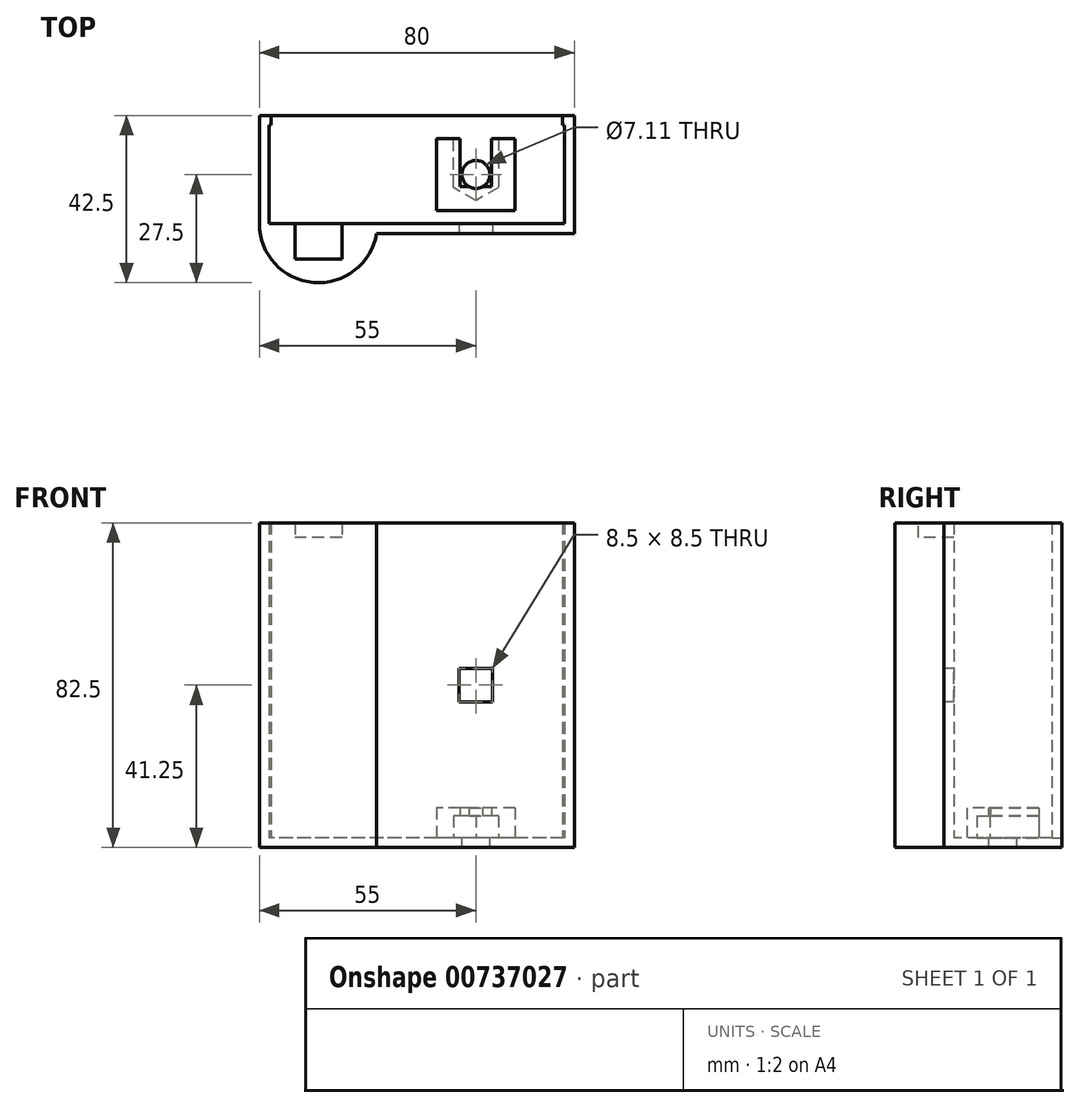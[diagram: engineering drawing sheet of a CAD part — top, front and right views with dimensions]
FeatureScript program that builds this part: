
annotation { "Feature Type Name" : "Feature", "Feature Type Description" : "" }
export const myFeature = defineFeature(function(context is Context, id is Id, definition is map)
    precondition{}
    {
        {
            assignVariable(context, id + "F0", {"name" : "shell_thickness", "anyValue" : 2.5 * mm});
        }
        {
            var Q0;
            Q0=qCreatedBy(makeId("Top.planeOp"),FACE);
            var sketch = newSketch(context, id + "F1", { "sketchPlane" : qUnion([Q0])});
            skLineSegment(sketch, "E0.bottom", {"start": v(37.5, 12.5) * mm, "end": v(-37.5, 12.5) * mm});
            skLineSegment(sketch, "E0.top", {"start": v(37.5, -12.5) * mm, "end": v(-37.5, -12.5) * mm});
            skLineSegment(sketch, "E0.left", {"start": v(37.5, 12.5) * mm, "end": v(37.5, -12.5) * mm});
            skLineSegment(sketch, "E0.right", {"start": v(-37.5, 12.5) * mm, "end": v(-37.5, -12.5) * mm});
            skPoint(sketch, "E0.middle", {"position": v(0, 0) * mm});
            skArc(sketch, "E1", {"start": v(-37.5, -12.5) * mm, "mid": v(-25, -25) * mm, "end": v(-12.5, -12.5) * mm});
            skLineSegment(sketch, "E2.0", {"start": v(-40, 15) * mm, "end": v(-40, -12.5) * mm});
            skLineSegment(sketch, "E2.1", {"start": v(40, 15) * mm, "end": v(-40, 15) * mm});
            skArc(sketch, "E2.2", {"start": v(-40, -12.5) * mm, "mid": v(-26.25, -27.45) * mm, "end": v(-10.2, -15) * mm});
            skLineSegment(sketch, "E2.3", {"start": v(40, -15) * mm, "end": v(-10.2, -15) * mm});
            skLineSegment(sketch, "E2.4", {"start": v(40, 15) * mm, "end": v(40, -15) * mm});
            skLineSegment(sketch, "E3", {"start": v(-37, 12.5) * mm, "end": v(-37, 15) * mm});
            skLineSegment(sketch, "E4", {"start": v(37, 12.5) * mm, "end": v(37, 15) * mm});
            skSolve(sketch);
        }
        {
            var Q0;
            Q0=makeQuery(id+"F1.imprint","IMPRINT",FACE,{"disambiguationData":[TD([[makeQuery(id+"F1.imprint","IMPRINT",EDGE,{"derivedFrom":sQuery(id+"F1.wireOp",EDGE,"E0.bottom")}),1.0]])]});
            var Q1;
            Q1=makeQuery(id+"F1.imprint","IMPRINT",FACE,{"disambiguationData":[TD([[makeQuery(id+"F1.imprint","IMPRINT",EDGE,{"derivedFrom":sQuery(id+"F1.wireOp",EDGE,"E0.bottom")}),-1.0]])]});
            var Q2;
            {var subQ0=sQuery(id+"F1.wireOp",EDGE,"E3");Q2=makeQuery(id+"F1.imprint","IMPRINT",FACE,{"disambiguationData":[TD([[makeQuery(id+"F1.imprint","IMPRINT",EDGE,{"derivedFrom":subQ0}),-1.0]])]});}
            var Q3;
            {var subQ0=sQuery(id+"F1.wireOp",EDGE,"E1");Q3=makeQuery(id+"F1.imprint","IMPRINT",FACE,{"disambiguationData":[TD([[makeQuery(id+"F1.imprint","IMPRINT",EDGE,{"derivedFrom":subQ0}),1.0]])]});}
            extrude(context, id + "F2", {"entities" : qUnion([Q0, Q1, Q2, Q3]), "oppositeDirection" : true, "depth" : getVariable(context, 'shell_thickness'), "offsetDistance" : 25 * mm});
        }
        {
            var Q0;
            {var subQ7=sQuery(id+"F1.wireOp",EDGE,"E0.left");Q0=makeQuery(id+"F1.imprint","IMPRINT",FACE,{"disambiguationData":[TD([[makeQuery(id+"F1.imprint","IMPRINT",EDGE,{"derivedFrom":subQ7}),1.0]])]});}
            var Q1;
            {var subQ0=sQuery(id+"F1.wireOp",EDGE,"E1");Q1=makeQuery(id+"F1.imprint","IMPRINT",FACE,{"disambiguationData":[TD([[makeQuery(id+"F1.imprint","IMPRINT",EDGE,{"derivedFrom":subQ0}),1.0]])]});}
            extrude(context, id + "F3", {"entities" : qUnion([Q0, Q1]), "operationType" : NewBodyOperationType.ADD, "depth" : 80 * mm, "offsetDistance" : 25 * mm});
        }
        {
            var Q0;
            Q0=makeQuery(id+"F3.opExtrude","CAP_FACE",FACE,{"disambiguationData":[OSD([sQuery(id+"F1.wireOp",EDGE,"E0.bottom"),sQuery(id+"F1.wireOp",EDGE,"E0.top"),sQuery(id+"F1.wireOp",EDGE,"E0.left"),sQuery(id+"F1.wireOp",EDGE,"E0.right"),sQuery(id+"F1.wireOp",EDGE,"E2.0"),sQuery(id+"F1.wireOp",EDGE,"E2.1"),sQuery(id+"F1.wireOp",EDGE,"E2.2"),sQuery(id+"F1.wireOp",EDGE,"E2.3"),sQuery(id+"F1.wireOp",EDGE,"E2.4"),sQuery(id+"F1.wireOp",EDGE,"E3"),sQuery(id+"F1.wireOp",EDGE,"E4")])],"isStart":false});
            var sketch = newSketch(context, id + "F4", { "sketchPlane" : qUnion([Q0])});
            skCircle(sketch, "E5", {"center": v(-25, -12.5) * mm, "radius": 12.5 * mm, "construction": true});
            skLineSegment(sketch, "E6.bottom", {"start": v(-19, -9.5) * mm, "end": v(-31, -9.5) * mm});
            skLineSegment(sketch, "E6.top", {"start": v(-19, -21.5) * mm, "end": v(-31, -21.5) * mm});
            skLineSegment(sketch, "E6.left", {"start": v(-19, -9.5) * mm, "end": v(-19, -21.5) * mm});
            skLineSegment(sketch, "E6.right", {"start": v(-31, -9.5) * mm, "end": v(-31, -21.5) * mm});
            skPoint(sketch, "E6.middle", {"position": v(-25, -15.5) * mm});
            skSolve(sketch);
        }
        {
            var Q0;
            Q0 = qSketchRegion(id + "F4", true);
            extrude(context, id + "F5", {"entities" : qUnion([Q0]), "operationType" : NewBodyOperationType.REMOVE, "oppositeDirection" : true, "depth" : 3.75 * mm, "offsetDistance" : 25 * mm});
        }
        {
            var Q0;
            {var subQ0=sQuery(id+"F1.wireOp",EDGE,"E2.3");Q0=makeQuery(id+"F3.boolean.opBoolean","MERGE",FACE,{"derivedFrom":[makeQuery(id+"F2.opExtrude","SWEPT_FACE",FACE,{"disambiguationData":[OSD([subQ0])]}),makeQuery(id+"F3.opExtrude","SWEPT_FACE",FACE,{"disambiguationData":[OSD([subQ0])]})]});}
            var sketch = newSketch(context, id + "F6", { "sketchPlane" : qUnion([Q0])});
            skPoint(sketch, "E7.middle.positionSnap0", {"position": v(40, 38.75) * mm});
            skPoint(sketch, "E7.middle.positionSnap1", {"position": v(14.9, -2.5) * mm});
            skPoint(sketch, "E7.centerSnap0", {"position": v(40, 38.75) * mm});
            skPoint(sketch, "E7.centerSnap1", {"position": v(14.9, -2.5) * mm});
            skLineSegment(sketch, "E8.bottom", {"start": v(19.25, 43) * mm, "end": v(10.75, 43) * mm});
            skLineSegment(sketch, "E8.top", {"start": v(19.25, 34.5) * mm, "end": v(10.75, 34.5) * mm});
            skLineSegment(sketch, "E8.left", {"start": v(19.25, 43) * mm, "end": v(19.25, 34.5) * mm});
            skLineSegment(sketch, "E8.right", {"start": v(10.75, 43) * mm, "end": v(10.75, 34.5) * mm});
            skPoint(sketch, "E8.middle", {"position": v(15, 38.75) * mm});
            skSolve(sketch);
        }
        {
            var Q0;
            Q0=makeQuery(id+"F6.imprint","IMPRINT",FACE,{"disambiguationData":[TD([[makeQuery(id+"F6.imprint","IMPRINT",EDGE,{"derivedFrom":sQuery(id+"F6.wireOp",EDGE,"E8.bottom")}),1.0]])]});
            extrude(context, id + "F7", {"entities" : qUnion([Q0]), "operationType" : NewBodyOperationType.REMOVE, "endBound" : BoundingType.UP_TO_NEXT, "oppositeDirection" : true, "depth" : 25 * mm, "offsetDistance" : 25 * mm});
        }
        {
            var Q0;
            {var subQ0=sQuery(id+"F1.wireOp",EDGE,"E0.left");Q0=makeQuery(id+"F1.imprint","IMPRINT",FACE,{"disambiguationData":[TD([[makeQuery(id+"F1.imprint","IMPRINT",EDGE,{"derivedFrom":subQ0}),-1.0]])]});}
            var sketch = newSketch(context, id + "F8", { "sketchPlane" : qUnion([Q0])});
            skCircle(sketch, "E9.cCircle", {"center": v(15, 0) * mm, "radius": 5.72 * mm, "construction": true});
            skLineSegment(sketch, "E9.0", {"start": v(9.29, -3.3) * mm, "end": v(9.29, 3.3) * mm});
            skLineSegment(sketch, "E9.1", {"start": v(9.29, 3.3) * mm, "end": v(15, 6.6) * mm});
            skLineSegment(sketch, "E9.2", {"start": v(15, 6.6) * mm, "end": v(20.71, 3.3) * mm});
            skLineSegment(sketch, "E9.3", {"start": v(20.71, 3.3) * mm, "end": v(20.71, -3.3) * mm});
            skLineSegment(sketch, "E9.4", {"start": v(20.71, -3.3) * mm, "end": v(15, -6.6) * mm});
            skLineSegment(sketch, "E9.5", {"start": v(15, -6.6) * mm, "end": v(9.29, -3.3) * mm});
            skPoint(sketch, "E9.0.midPoint", {"position": v(9.29, 0) * mm});
            skCircle(sketch, "E10", {"center": v(15, 0) * mm, "radius": 3.56 * mm});
            skLineSegment(sketch, "E11.bottom", {"start": v(25, 9.11) * mm, "end": v(19, 9.11) * mm});
            skLineSegment(sketch, "E11.top", {"start": v(25, -9.11) * mm, "end": v(5, -9.11) * mm});
            skLineSegment(sketch, "E11.left", {"start": v(25, 9.11) * mm, "end": v(25, -9.11) * mm});
            skLineSegment(sketch, "E11.right", {"start": v(5, 9.11) * mm, "end": v(5, -9.11) * mm});
            skLineSegment(sketch, "E12.top", {"start": v(19, -3.11) * mm, "end": v(11, -3.11) * mm});
            skLineSegment(sketch, "E12.left", {"start": v(19, 3.11) * mm, "end": v(19, -3.11) * mm});
            skLineSegment(sketch, "E12.right", {"start": v(11, 3.11) * mm, "end": v(11, -3.11) * mm});
            skLineSegment(sketch, "E13", {"start": v(11, 3.11) * mm, "end": v(11, 9.11) * mm});
            skLineSegment(sketch, "E14", {"start": v(19, 3.11) * mm, "end": v(19, 9.11) * mm});
            skLineSegment(sketch, "E15.trimOffspring", {"start": v(11, 9.11) * mm, "end": v(5, 9.11) * mm});
            skLineSegment(sketch, "E16", {"start": v(9.29, 3.3) * mm, "end": v(9.29, 9.11) * mm});
            skLineSegment(sketch, "E17", {"start": v(20.71, 3.3) * mm, "end": v(20.71, 9.11) * mm});
            skSolve(sketch);
        }
        {
            var Q0;
            {var subQ0=sQuery(id+"F8.wireOp",EDGE,"E12.top");var subQ1=sQuery(id+"F8.wireOp",EDGE,"E10");var subQ2=makeQuery(id+"F8.imprint","INTERSECT",VERTEX,{"disambiguationData":[OD(0.0)],"derivedFrom":[subQ1,subQ0]});Q0=makeQuery(id+"F8.imprint","IMPRINT",FACE,{"disambiguationData":[TD([[makeQuery(id+"F8.imprint","IMPRINT",EDGE,{"disambiguationData":[TD([[subQ2,-1.0]])],"derivedFrom":subQ1}),1.0]])]});}
            var Q1;
            {var subQ0=sQuery(id+"F8.wireOp",EDGE,"E12.top");var subQ1=sQuery(id+"F8.wireOp",EDGE,"E10");var subQ2=makeQuery(id+"F8.imprint","INTERSECT",VERTEX,{"disambiguationData":[OD(0.0)],"derivedFrom":[subQ1,subQ0]});Q1=makeQuery(id+"F8.imprint","IMPRINT",FACE,{"disambiguationData":[TD([[makeQuery(id+"F8.imprint","IMPRINT",EDGE,{"disambiguationData":[TD([[subQ2,1.0]])],"derivedFrom":subQ1}),1.0]])]});}
            extrude(context, id + "F9", {"entities" : qUnion([Q0, Q1]), "operationType" : NewBodyOperationType.REMOVE, "endBound" : BoundingType.UP_TO_NEXT, "oppositeDirection" : true, "depth" : 25 * mm, "offsetDistance" : 25 * mm});
        }
        {
            var Q0;
            Q0=makeQuery(id+"F8.imprint","IMPRINT",FACE,{"disambiguationData":[TD([[makeQuery(id+"F8.imprint","IMPRINT",EDGE,{"derivedFrom":sQuery(id+"F8.wireOp",EDGE,"E9.0")}),1.0]])]});
            var Q1;
            {var subQ0=sQuery(id+"F8.wireOp",EDGE,"E17");Q1=makeQuery(id+"F8.imprint","IMPRINT",FACE,{"disambiguationData":[TD([[makeQuery(id+"F8.imprint","IMPRINT",EDGE,{"derivedFrom":subQ0}),1.0]])]});}
            var Q2;
            {var subQ6=sQuery(id+"F8.wireOp",EDGE,"E9.0");Q2=makeQuery(id+"F8.imprint","IMPRINT",FACE,{"disambiguationData":[TD([[makeQuery(id+"F8.imprint","IMPRINT",EDGE,{"derivedFrom":subQ6}),-1.0]])]});}
            var Q3;
            {var subQ0=sQuery(id+"F8.wireOp",EDGE,"E16");Q3=makeQuery(id+"F8.imprint","IMPRINT",FACE,{"disambiguationData":[TD([[makeQuery(id+"F8.imprint","IMPRINT",EDGE,{"derivedFrom":subQ0}),-1.0]])]});}
            extrude(context, id + "F10", {"entities" : qUnion([Q0, Q1, Q2, Q3]), "operationType" : NewBodyOperationType.ADD, "depth" : 7.62 * mm, "offsetDistance" : 25 * mm});
        }
        {
            var Q0;
            {var subQ6=sQuery(id+"F8.wireOp",EDGE,"E9.0");Q0=makeQuery(id+"F8.imprint","IMPRINT",FACE,{"disambiguationData":[TD([[makeQuery(id+"F8.imprint","IMPRINT",EDGE,{"derivedFrom":subQ6}),-1.0]])]});}
            var Q1;
            {var subQ0=sQuery(id+"F8.wireOp",EDGE,"E17");Q1=makeQuery(id+"F8.imprint","IMPRINT",FACE,{"disambiguationData":[TD([[makeQuery(id+"F8.imprint","IMPRINT",EDGE,{"derivedFrom":subQ0}),1.0]])]});}
            var Q2;
            {var subQ0=sQuery(id+"F8.wireOp",EDGE,"E16");Q2=makeQuery(id+"F8.imprint","IMPRINT",FACE,{"disambiguationData":[TD([[makeQuery(id+"F8.imprint","IMPRINT",EDGE,{"derivedFrom":subQ0}),-1.0]])]});}
            extrude(context, id + "F11", {"entities" : qUnion([Q0, Q1, Q2]), "operationType" : NewBodyOperationType.REMOVE, "depth" : 5.6 * mm, "offsetDistance" : 25 * mm});
        }
    });
